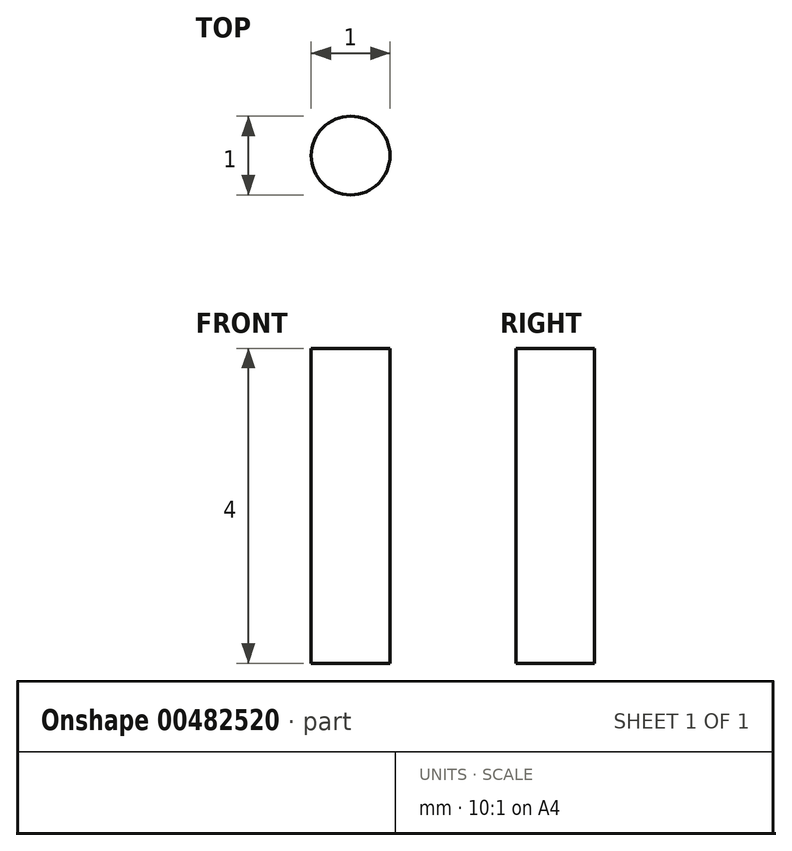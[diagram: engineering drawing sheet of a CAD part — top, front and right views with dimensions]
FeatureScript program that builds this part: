
annotation { "Feature Type Name" : "Feature", "Feature Type Description" : "" }
export const myFeature = defineFeature(function(context is Context, id is Id, definition is map)
    precondition{}
    {
        {
            var Q0;
            Q0=qCreatedBy(makeId("Top.planeOp"),FACE);
            var sketch = newSketch(context, id + "F0", { "sketchPlane" : qUnion([Q0])});
            skCircle(sketch, "E0", {"center": v(0, 0) * mm, "radius": 0.5 * mm});
            skSolve(sketch);
        }
        {
            var Q0;
            Q0=makeQuery(id+"F0.imprint","IMPRINT",FACE,{"disambiguationData":[TD([[makeQuery(id+"F0.imprint","IMPRINT",EDGE,{"derivedFrom":sQuery(id+"F0.wireOp",EDGE,"E0")}),1.0]])]});
            extrude(context, id + "F1", {"entities" : qUnion([Q0]), "oppositeDirection" : true, "depth" : 4 * mm});
        }
    });
